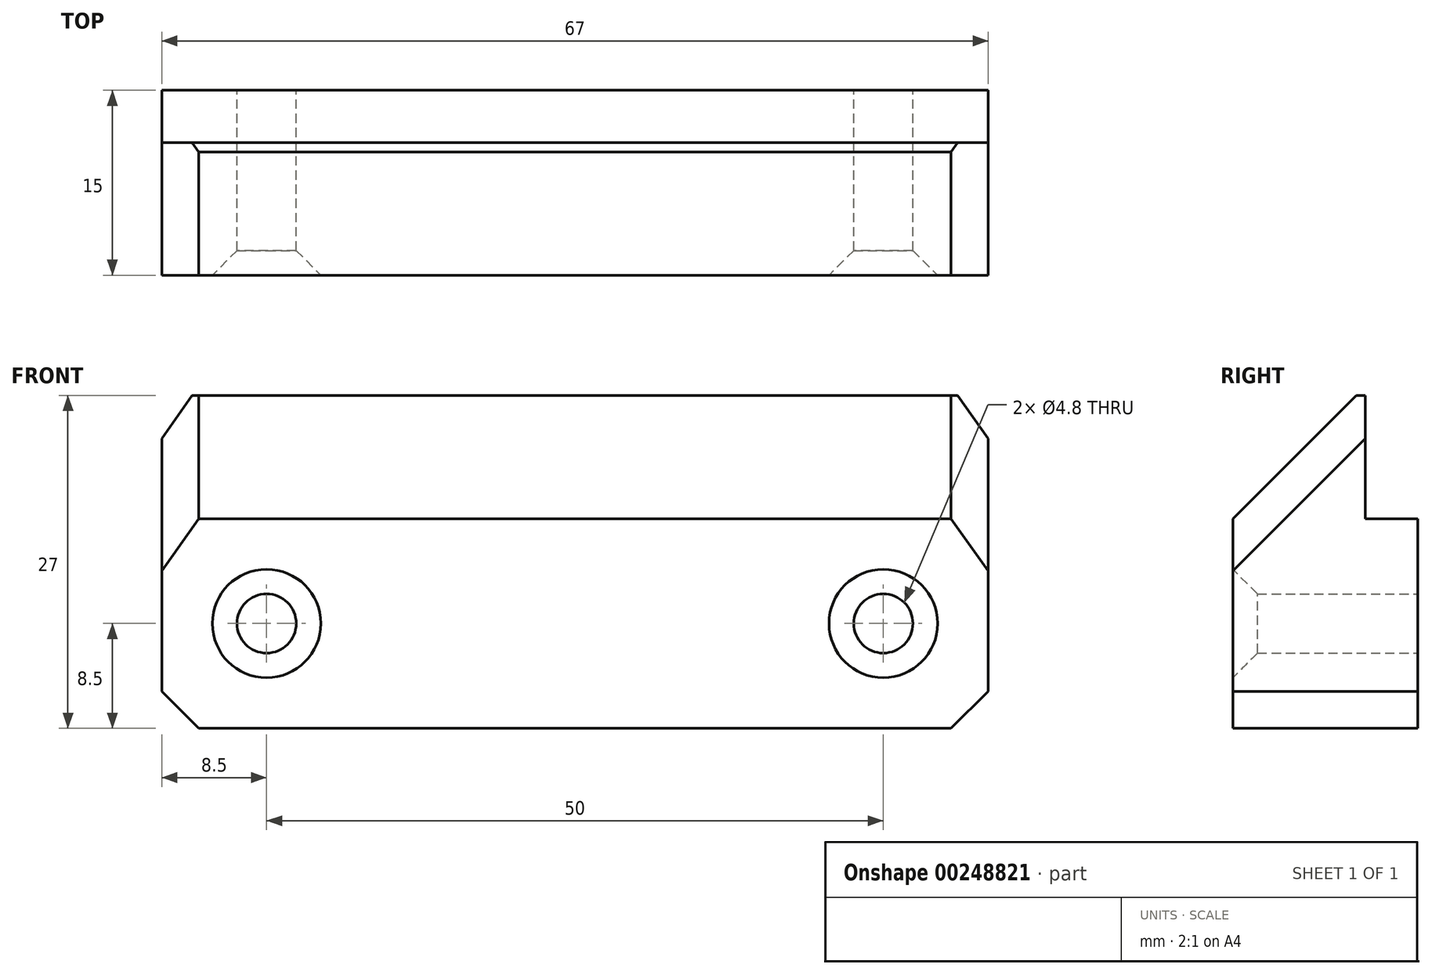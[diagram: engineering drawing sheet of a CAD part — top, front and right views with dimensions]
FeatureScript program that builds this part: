
annotation { "Feature Type Name" : "Feature", "Feature Type Description" : "" }
export const myFeature = defineFeature(function(context is Context, id is Id, definition is map)
    precondition{}
    {
        {
            var Q0;
            Q0=qCreatedBy(makeId("Front.planeOp"),FACE);
            var sketch = newSketch(context, id + "F0", { "sketchPlane" : qUnion([Q0])});
            skCircle(sketch, "E0", {"center": v(-25, 0) * mm, "radius": 2.4 * mm});
            skCircle(sketch, "E1.MirrorC", {"center": v(25, 0) * mm, "radius": 2.4 * mm});
            skLineSegment(sketch, "E2.bottom", {"start": v(-33.5, 8.5) * mm, "end": v(33.5, 8.5) * mm});
            skLineSegment(sketch, "E2.top", {"start": v(-33.5, -8.5) * mm, "end": v(33.5, -8.5) * mm});
            skLineSegment(sketch, "E2.left", {"start": v(-33.5, 8.5) * mm, "end": v(-33.5, -8.5) * mm});
            skLineSegment(sketch, "E2.right", {"start": v(33.5, 8.5) * mm, "end": v(33.5, -8.5) * mm});
            skPoint(sketch, "E2.middle", {"position": v(0, 0) * mm});
            skLineSegment(sketch, "E3", {"start": v(-33.5, 8.5) * mm, "end": v(-33.5, 18.5) * mm});
            skLineSegment(sketch, "E4", {"start": v(-33.5, 18.5) * mm, "end": v(33.5, 18.5) * mm});
            skLineSegment(sketch, "E5", {"start": v(33.5, 18.5) * mm, "end": v(33.5, 8.5) * mm});
            skSolve(sketch);
        }
        {
            var Q0;
            Q0=makeQuery(id+"F0.imprint","IMPRINT",FACE,{"disambiguationData":[TD([[makeQuery(id+"F0.imprint","IMPRINT",EDGE,{"derivedFrom":sQuery(id+"F0.wireOp",EDGE,"E0")}),-1.0]])]});
            var Q1;
            Q1=makeQuery(id+"F0.imprint","IMPRINT",FACE,{"disambiguationData":[TD([[makeQuery(id+"F0.imprint","IMPRINT",EDGE,{"derivedFrom":sQuery(id+"F0.wireOp",EDGE,"E2.bottom")}),1.0]])]});
            extrude(context, id + "F1", {"entities" : qUnion([Q0, Q1]), "depth" : 15 * mm});
        }
        {
            var Q0;
            Q0=makeQuery(id+"F0.imprint","IMPRINT",FACE,{"disambiguationData":[TD([[makeQuery(id+"F0.imprint","IMPRINT",EDGE,{"derivedFrom":sQuery(id+"F0.wireOp",EDGE,"E2.bottom")}),1.0]])]});
            extrude(context, id + "F2", {"entities" : qUnion([Q0]), "operationType" : NewBodyOperationType.REMOVE, "depth" : 4.25 * mm});
        }
        {
            var Q0;
            Q0=makeQuery(id+"F1.opExtrude","CAP_EDGE",EDGE,{"disambiguationData":[OSD([sQuery(id+"F0.wireOp",EDGE,"E0")])],"isStart":false});
            var Q1;
            Q1=makeQuery(id+"F1.opExtrude","CAP_EDGE",EDGE,{"disambiguationData":[OSD([sQuery(id+"F0.wireOp",EDGE,"E1.MirrorC")])],"isStart":false});
            chamfer(context, id + "F3", {"entities" : qUnion([Q0, Q1]), "width" : 2 * mm, "tangentPropagation" : true});
        }
        {
            var Q0;
            Q0=makeQuery(id+"F1.opExtrude","CAP_EDGE",EDGE,{"disambiguationData":[OSD([sQuery(id+"F0.wireOp",EDGE,"E4")])],"isStart":false});
            chamfer(context, id + "F4", {"entities" : qUnion([Q0]), "width" : 10 * mm, "tangentPropagation" : true});
        }
        {
            var Q0;
            Q0=makeQuery(id+"F4.opChamfer","BLEND_EDGE",EDGE,{"blendedFrom":[makeQuery(id+"F1.opExtrude","CAP_EDGE",EDGE,{"disambiguationData":[OSD([sQuery(id+"F0.wireOp",EDGE,"E4")])],"isStart":false}),makeQuery(id+"F1.opExtrude","SWEPT_FACE",FACE,{"disambiguationData":[OSD([sQuery(id+"F0.wireOp",EDGE,"E2.left"),sQuery(id+"F0.wireOp",EDGE,"E3")])]})],"blendedInto":[makeQuery(id+"F1.opExtrude","SWEPT_FACE",FACE,{"disambiguationData":[OSD([sQuery(id+"F0.wireOp",EDGE,"E2.left"),sQuery(id+"F0.wireOp",EDGE,"E3")])]})]});
            var Q1;
            Q1=makeQuery(id+"F4.opChamfer","BLEND_EDGE",EDGE,{"blendedFrom":[makeQuery(id+"F1.opExtrude","CAP_EDGE",EDGE,{"disambiguationData":[OSD([sQuery(id+"F0.wireOp",EDGE,"E4")])],"isStart":false}),makeQuery(id+"F1.opExtrude","SWEPT_FACE",FACE,{"disambiguationData":[OSD([sQuery(id+"F0.wireOp",EDGE,"E2.right"),sQuery(id+"F0.wireOp",EDGE,"E5")])]})],"blendedInto":[makeQuery(id+"F1.opExtrude","SWEPT_FACE",FACE,{"disambiguationData":[OSD([sQuery(id+"F0.wireOp",EDGE,"E2.right"),sQuery(id+"F0.wireOp",EDGE,"E5")])]})]});
            var Q2;
            Q2=makeQuery(id+"F1.opExtrude","SWEPT_EDGE",EDGE,{"disambiguationData":[OSD([sQuery(id+"F0.wireOp",EDGE,"E2.top"),sQuery(id+"F0.wireOp",EDGE,"E2.right")])]});
            var Q3;
            Q3=makeQuery(id+"F1.opExtrude","SWEPT_EDGE",EDGE,{"disambiguationData":[OSD([sQuery(id+"F0.wireOp",EDGE,"E2.top"),sQuery(id+"F0.wireOp",EDGE,"E2.left")])]});
            var Q4;
            Q4=makeQuery(id+"F2.boolean.opBoolean","COPY",EDGE,{"derivedFrom":makeQuery(id+"F2.opExtrude","SWEPT_EDGE",EDGE,{"disambiguationData":[OSD([sQuery(id+"F0.wireOp",EDGE,"E2.bottom"),sQuery(id+"F0.wireOp",EDGE,"E2.right"),sQuery(id+"F0.wireOp",EDGE,"E5")])]})});
            var Q5;
            Q5=makeQuery(id+"F2.boolean.opBoolean","COPY",EDGE,{"derivedFrom":makeQuery(id+"F2.opExtrude","CAP_EDGE",EDGE,{"disambiguationData":[OSD([sQuery(id+"F0.wireOp",EDGE,"E5")])],"isStart":false})});
            var Q6;
            Q6=makeQuery(id+"F2.boolean.opBoolean","COPY",EDGE,{"derivedFrom":makeQuery(id+"F2.opExtrude","CAP_EDGE",EDGE,{"disambiguationData":[OSD([sQuery(id+"F0.wireOp",EDGE,"E3")])],"isStart":false})});
            var Q7;
            Q7=makeQuery(id+"F2.boolean.opBoolean","COPY",EDGE,{"derivedFrom":makeQuery(id+"F2.opExtrude","SWEPT_EDGE",EDGE,{"disambiguationData":[OSD([sQuery(id+"F0.wireOp",EDGE,"E2.bottom"),sQuery(id+"F0.wireOp",EDGE,"E2.left"),sQuery(id+"F0.wireOp",EDGE,"E3")])]})});
            chamfer(context, id + "F5", {"entities" : qUnion([Q0, Q1, Q2, Q3, Q4, Q5, Q6, Q7]), "width" : 3 * mm, "tangentPropagation" : true});
        }
    });
